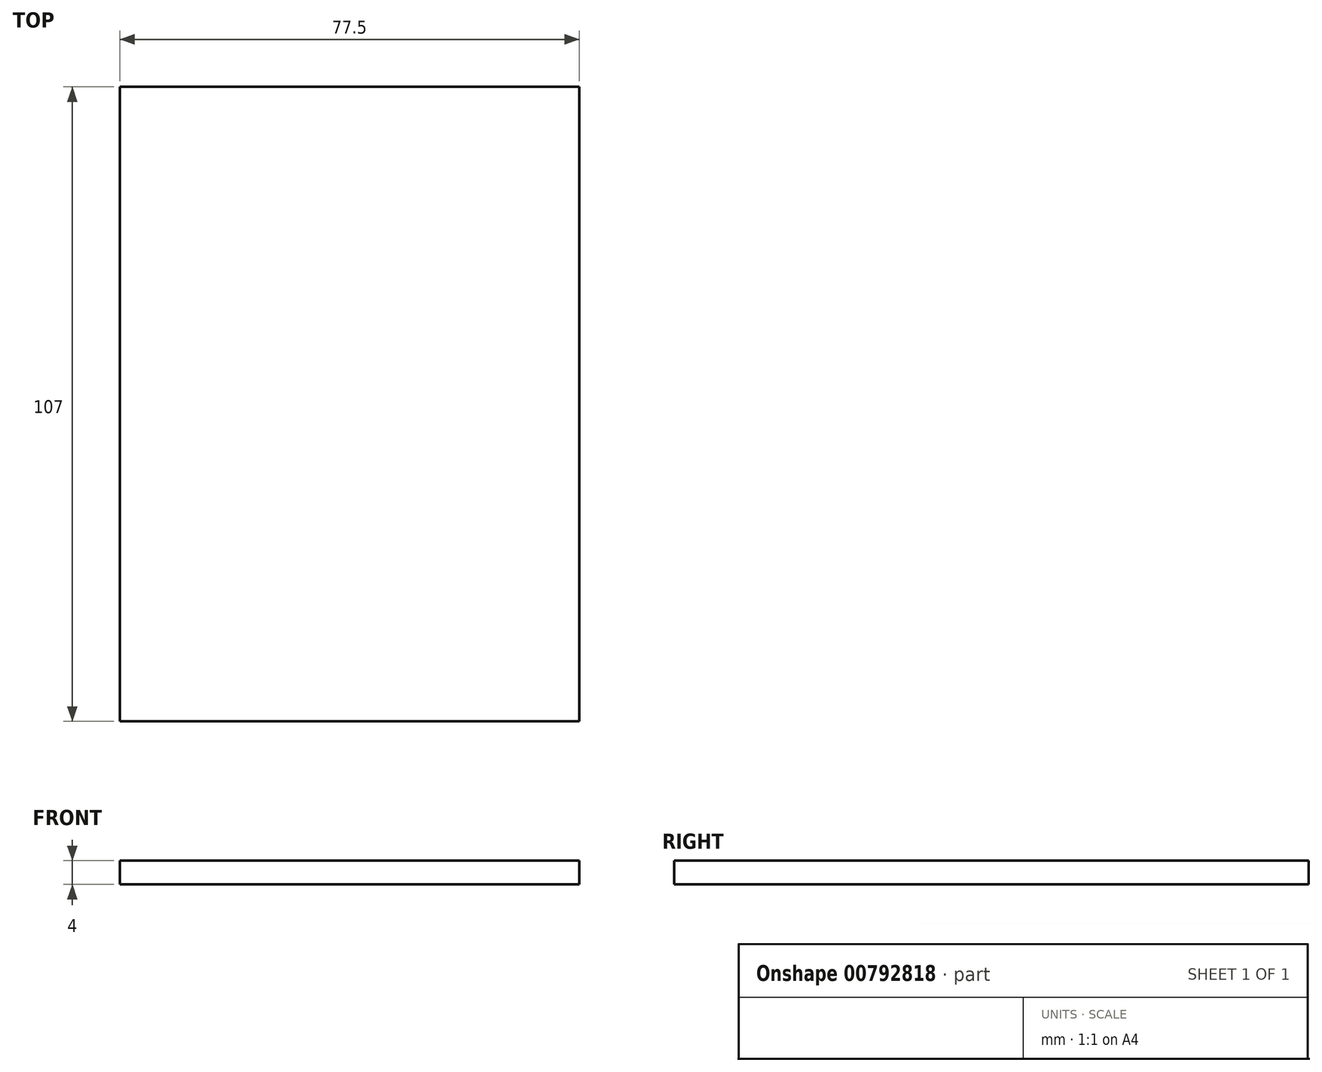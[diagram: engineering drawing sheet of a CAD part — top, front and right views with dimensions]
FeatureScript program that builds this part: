
annotation { "Feature Type Name" : "Feature", "Feature Type Description" : "" }
export const myFeature = defineFeature(function(context is Context, id is Id, definition is map)
    precondition{}
    {
        {
            var Q0;
            Q0=qCreatedBy(makeId("Top.planeOp"),FACE);
            var sketch = newSketch(context, id + "F0", { "sketchPlane" : qUnion([Q0])});
            skLineSegment(sketch, "E0.bottom", {"start": v(38.75, 309.5) * mm, "end": v(-38.75, 309.5) * mm});
            skLineSegment(sketch, "E0.top", {"start": v(38.75, -309.5) * mm, "end": v(-38.75, -309.5) * mm});
            skLineSegment(sketch, "E0.left", {"start": v(38.75, 309.5) * mm, "end": v(38.75, -309.5) * mm});
            skLineSegment(sketch, "E0.right", {"start": v(-38.75, 309.5) * mm, "end": v(-38.75, -309.5) * mm});
            skPoint(sketch, "E0.middle", {"position": v(0, 0) * mm});
            skSolve(sketch);
        }
        {
            var Q0;
            Q0 = qSketchRegion(id + "F0", true);
            extrude(context, id + "F1", {"entities" : qUnion([Q0]), "depth" : 4 * mm, "offsetDistance" : 25 * mm});
        }
        {
            var Q0;
            Q0=makeQuery(id+"F1.opExtrude","CAP_FACE",FACE,{"disambiguationData":[OSD([sQuery(id+"F0.wireOp",EDGE,"E0.bottom"),sQuery(id+"F0.wireOp",EDGE,"E0.top"),sQuery(id+"F0.wireOp",EDGE,"E0.left"),sQuery(id+"F0.wireOp",EDGE,"E0.right")])],"isStart":false});
            var sketch = newSketch(context, id + "F2", { "sketchPlane" : qUnion([Q0])});
            skLineSegment(sketch, "E1", {"start": v(-70.26, -309.5) * mm, "end": v(63.13, -309.5) * mm});
            skPoint(sketch, "E1.endSnap0", {"position": v(0, -309.5) * mm});
            skLineSegment(sketch, "E2", {"start": v(63.13, -181.5) * mm, "end": v(-70.26, -181.5) * mm});
            skLineSegment(sketch, "E3", {"start": v(-70.26, -53.5) * mm, "end": v(63.13, -53.5) * mm});
            skLineSegment(sketch, "E4", {"start": v(63.13, 74.5) * mm, "end": v(-70.26, 74.5) * mm});
            skLineSegment(sketch, "E5", {"start": v(-70.26, 202.5) * mm, "end": v(63.13, 202.5) * mm});
            skLineSegment(sketch, "E6", {"start": v(-70.26, 309.5) * mm, "end": v(63.13, 309.5) * mm});
            skLineSegment(sketch, "E7", {"start": v(63.13, 309.5) * mm, "end": v(63.13, 202.5) * mm});
            skLineSegment(sketch, "E8", {"start": v(63.13, 202.5) * mm, "end": v(63.13, 74.5) * mm});
            skLineSegment(sketch, "E9", {"start": v(63.13, 74.5) * mm, "end": v(63.13, -53.5) * mm});
            skLineSegment(sketch, "E10", {"start": v(63.13, -53.5) * mm, "end": v(63.13, -181.5) * mm});
            skLineSegment(sketch, "E11", {"start": v(63.13, -181.5) * mm, "end": v(63.13, -309.5) * mm});
            skLineSegment(sketch, "E12", {"start": v(-70.26, -309.5) * mm, "end": v(-70.26, -181.5) * mm});
            skLineSegment(sketch, "E13", {"start": v(-70.26, -181.5) * mm, "end": v(-70.26, -53.5) * mm});
            skLineSegment(sketch, "E14", {"start": v(-70.26, -53.5) * mm, "end": v(-70.26, 74.5) * mm});
            skLineSegment(sketch, "E15", {"start": v(-70.26, 74.5) * mm, "end": v(-70.26, 202.5) * mm});
            skSolve(sketch);
        }
        {
            var Q0;
            Q0 = qSketchRegion(id + "F2", true);
            extrude(context, id + "F3", {"entities" : qUnion([Q0]), "operationType" : NewBodyOperationType.REMOVE, "oppositeDirection" : true, "depth" : 5 * mm, "offsetDistance" : 25 * mm});
        }
    });
